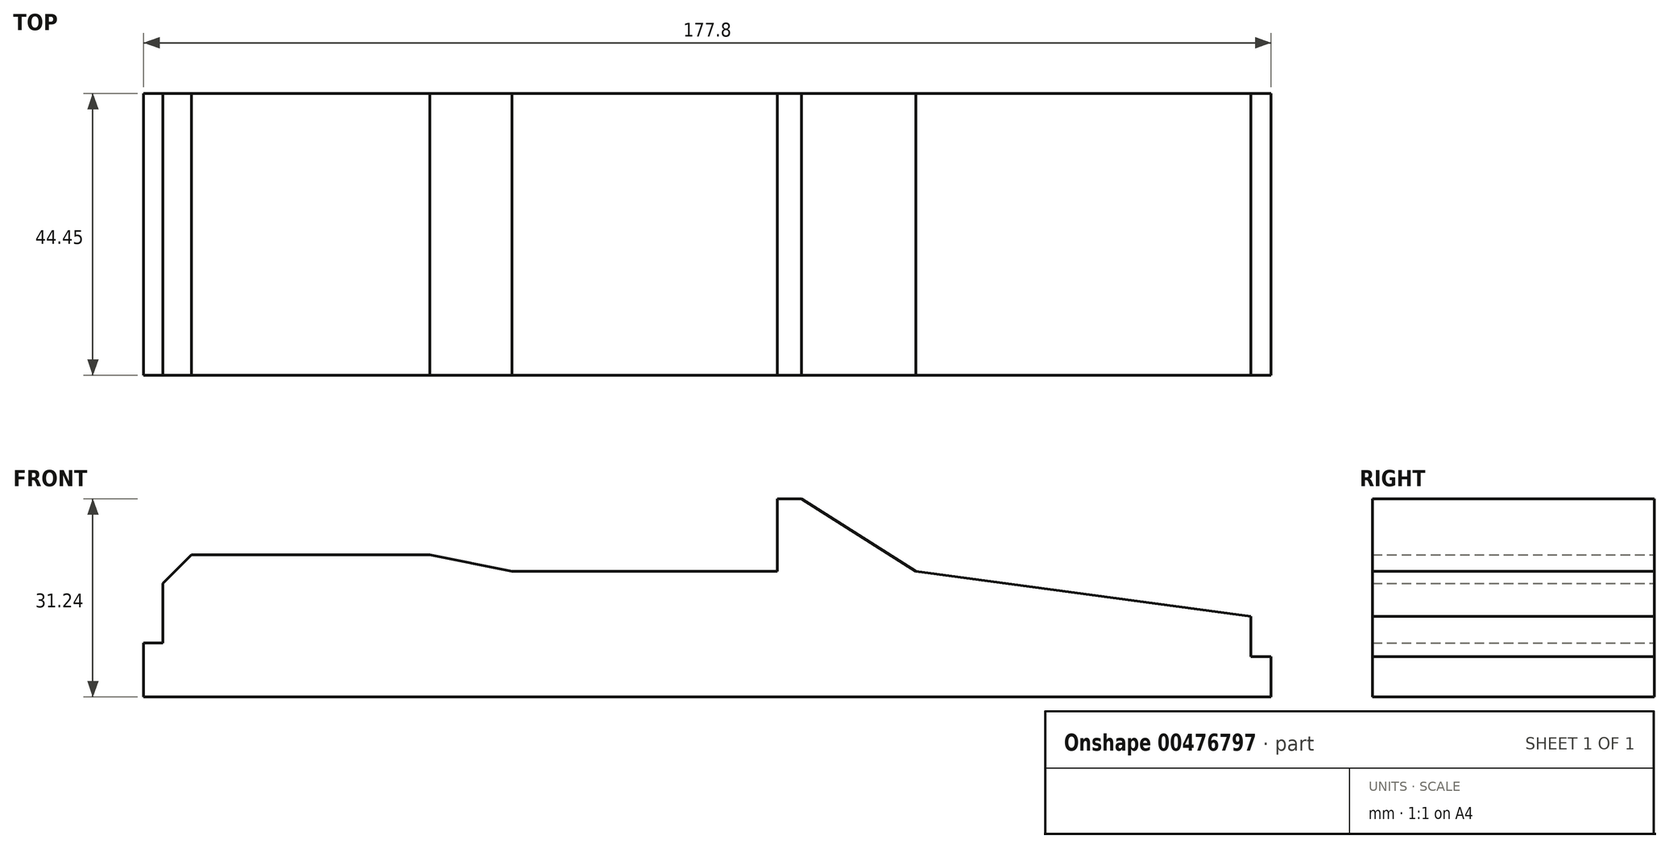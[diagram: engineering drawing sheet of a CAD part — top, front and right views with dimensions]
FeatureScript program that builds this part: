
annotation { "Feature Type Name" : "Feature", "Feature Type Description" : "" }
export const myFeature = defineFeature(function(context is Context, id is Id, definition is map)
    precondition{}
    {
        {
            var Q0;
            Q0=qCreatedBy(makeId("Front.planeOp"),FACE);
            var sketch = newSketch(context, id + "F0", { "sketchPlane" : qUnion([Q0])});
            skLineSegment(sketch, "E0", {"start": v(0, 0) * mm, "end": v(177.8, 0) * mm});
            skLineSegment(sketch, "E1", {"start": v(0, 0) * mm, "end": v(0, 8.5) * mm});
            skLineSegment(sketch, "E2", {"start": v(0, 8.5) * mm, "end": v(3.05, 8.5) * mm});
            skLineSegment(sketch, "E3", {"start": v(3.05, 8.5) * mm, "end": v(3.05, 17.9) * mm});
            skLineSegment(sketch, "E4", {"start": v(3.05, 17.9) * mm, "end": v(7.54, 22.4) * mm});
            skLineSegment(sketch, "E5", {"start": v(7.54, 22.4) * mm, "end": v(45.13, 22.4) * mm});
            skLineSegment(sketch, "E6", {"start": v(45.13, 22.4) * mm, "end": v(58.08, 19.81) * mm});
            skLineSegment(sketch, "E7", {"start": v(58.08, 19.81) * mm, "end": v(99.94, 19.81) * mm});
            skLineSegment(sketch, "E8", {"start": v(99.94, 19.81) * mm, "end": v(99.94, 31.24) * mm});
            skLineSegment(sketch, "E9", {"start": v(99.94, 31.24) * mm, "end": v(103.75, 31.24) * mm});
            skLineSegment(sketch, "E10", {"start": v(103.75, 31.24) * mm, "end": v(121.76, 19.81) * mm});
            skLineSegment(sketch, "E11", {"start": v(121.76, 19.81) * mm, "end": v(174.63, 12.7) * mm});
            skLineSegment(sketch, "E12", {"start": v(174.63, 12.7) * mm, "end": v(174.63, 6.35) * mm});
            skLineSegment(sketch, "E13", {"start": v(174.63, 6.35) * mm, "end": v(177.8, 6.35) * mm});
            skLineSegment(sketch, "E14", {"start": v(177.8, 6.35) * mm, "end": v(177.8, 0) * mm});
            skSolve(sketch);
        }
        {
            var Q0;
            Q0 = qSketchRegion(id + "F0", true);
            extrude(context, id + "F1", {"entities" : qUnion([Q0]), "depth" : 44.45 * mm});
        }
    });
